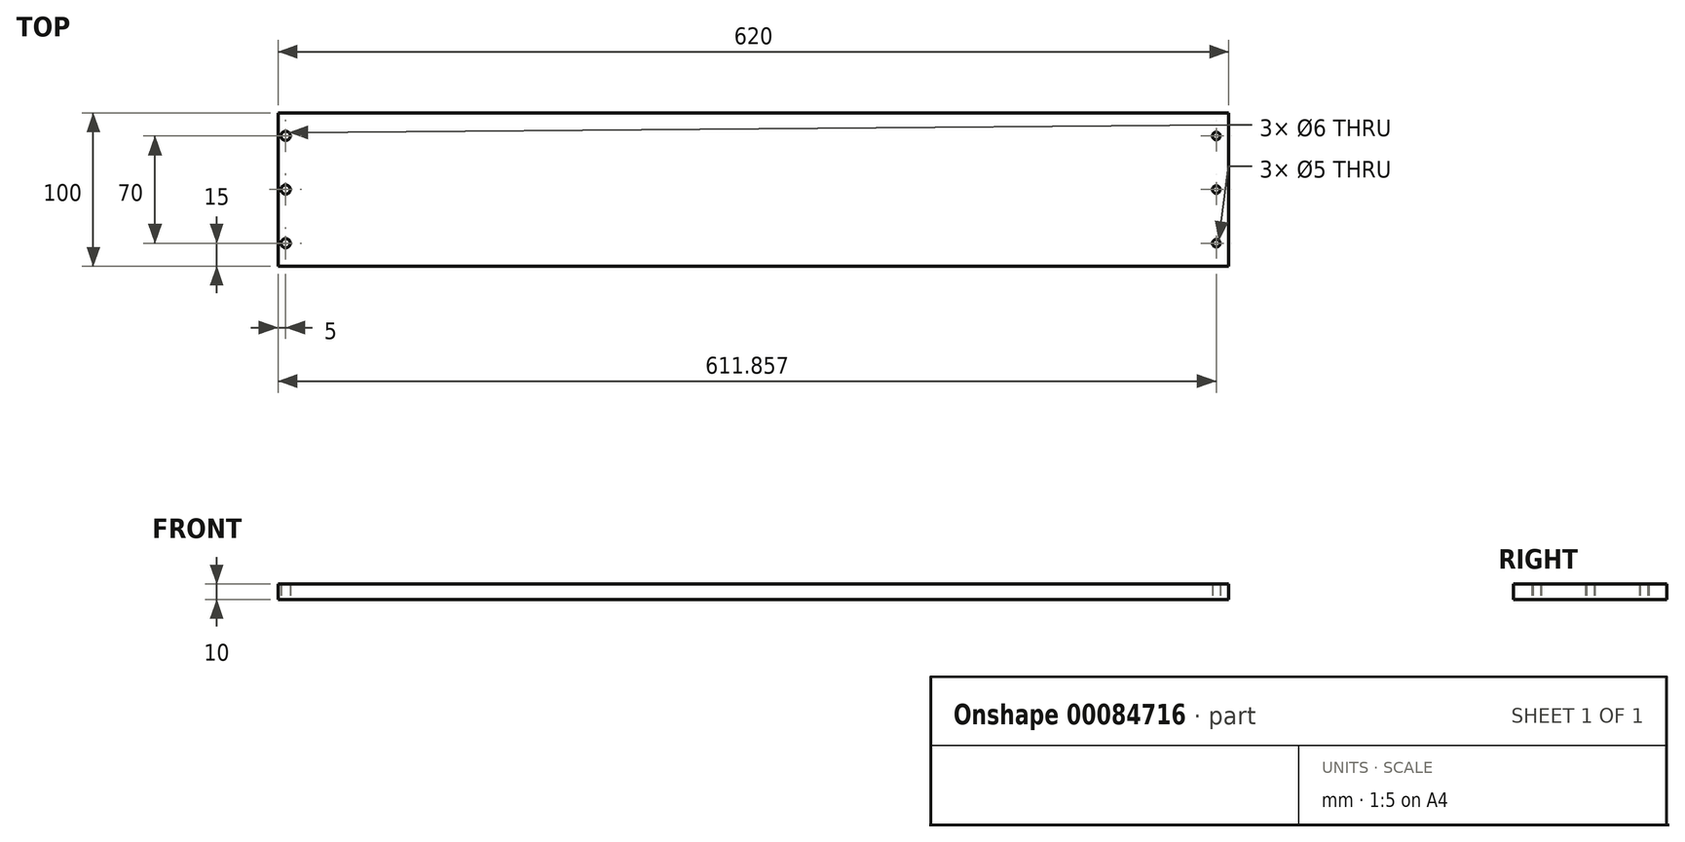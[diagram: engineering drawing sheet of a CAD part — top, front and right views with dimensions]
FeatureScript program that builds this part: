
annotation { "Feature Type Name" : "Feature", "Feature Type Description" : "" }
export const myFeature = defineFeature(function(context is Context, id is Id, definition is map)
    precondition{}
    {
        {
            var Q0;
            Q0=qCreatedBy(makeId("Top.planeOp"),FACE);
            var sketch = newSketch(context, id + "F0", { "sketchPlane" : qUnion([Q0])});
            skLineSegment(sketch, "E0.bottom", {"start": v(-310, 50) * mm, "end": v(310, 50) * mm});
            skLineSegment(sketch, "E0.top", {"start": v(-310, -50) * mm, "end": v(310, -50) * mm});
            skLineSegment(sketch, "E0.left", {"start": v(-310, 50) * mm, "end": v(-310, -50) * mm});
            skLineSegment(sketch, "E0.right", {"start": v(310, 50) * mm, "end": v(310, -50) * mm});
            skPoint(sketch, "E0.middle", {"position": v(0, 0) * mm});
            skCircle(sketch, "E1", {"center": v(-305, 35) * mm, "radius": 3 * mm});
            skCircle(sketch, "E2", {"center": v(-305, 0) * mm, "radius": 3 * mm});
            skCircle(sketch, "E3", {"center": v(-305, -35) * mm, "radius": 3 * mm});
            skCircle(sketch, "E4", {"center": v(301.86, 0) * mm, "radius": 2.5 * mm});
            skCircle(sketch, "E5", {"center": v(301.86, 35) * mm, "radius": 2.5 * mm});
            skCircle(sketch, "E6", {"center": v(301.86, -35) * mm, "radius": 2.5 * mm});
            skSolve(sketch);
        }
        {
            var Q0;
            Q0=makeQuery(id+"F0.imprint","IMPRINT",FACE,{"disambiguationData":[TD([[makeQuery(id+"F0.imprint","IMPRINT",EDGE,{"derivedFrom":sQuery(id+"F0.wireOp",EDGE,"E0.bottom")}),-1.0]])]});
            extrude(context, id + "F1", {"entities" : qUnion([Q0]), "depth" : 10 * mm});
        }
    });
